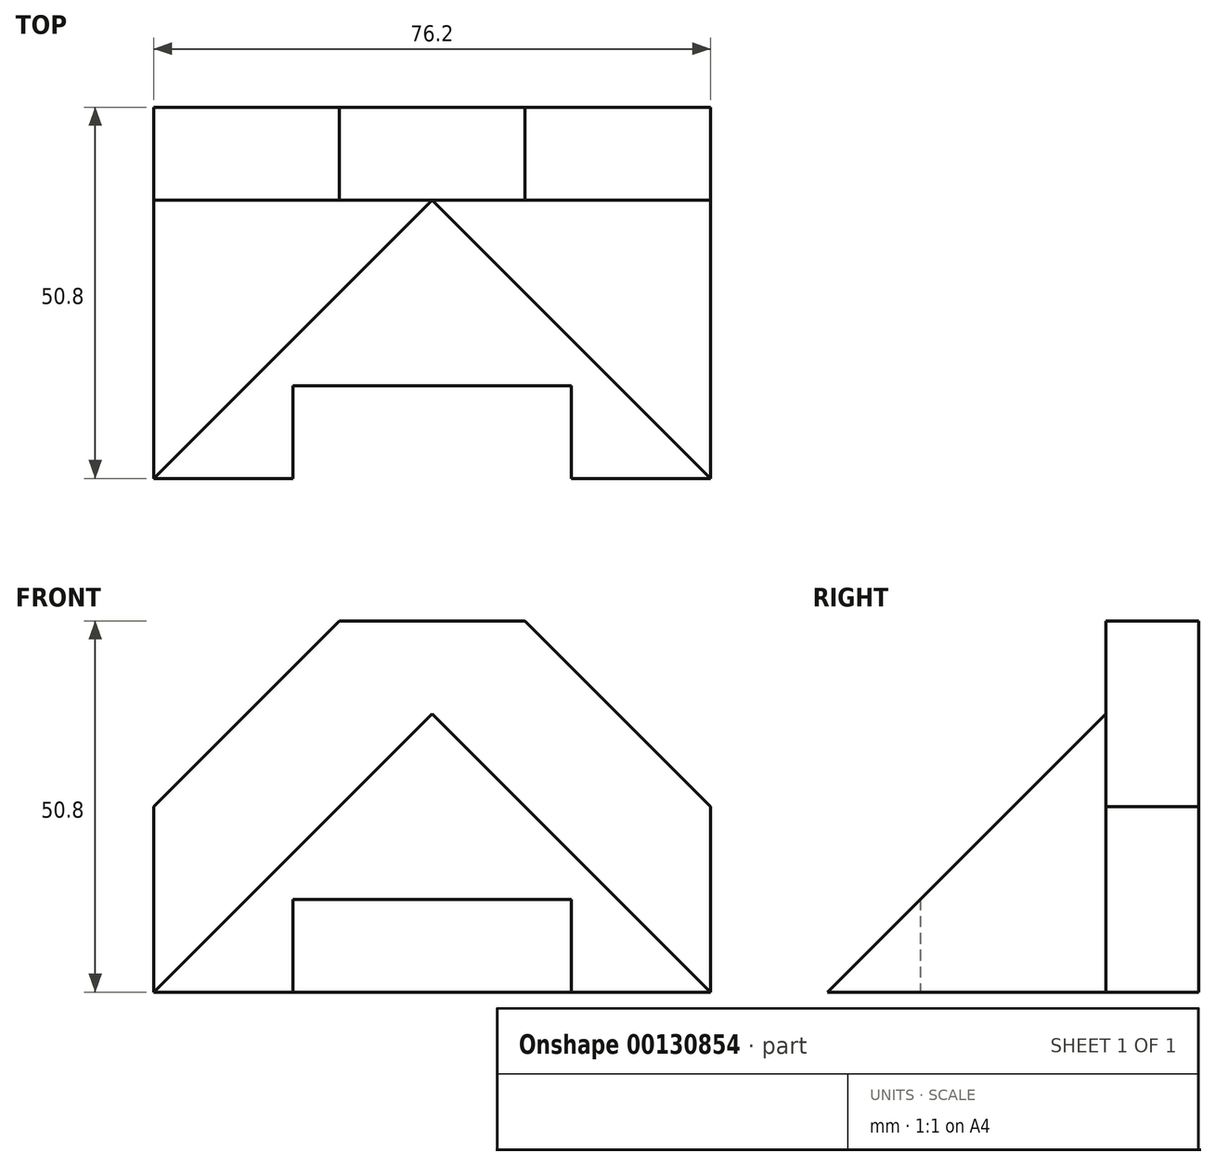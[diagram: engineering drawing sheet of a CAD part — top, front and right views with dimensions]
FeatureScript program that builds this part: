
annotation { "Feature Type Name" : "Feature", "Feature Type Description" : "" }
export const myFeature = defineFeature(function(context is Context, id is Id, definition is map)
    precondition{}
    {
        {
            var Q0;
            Q0=qCreatedBy(makeId("Right.planeOp"),FACE);
            var sketch = newSketch(context, id + "F0", { "sketchPlane" : qUnion([Q0])});
            skLineSegment(sketch, "E0", {"start": v(0, 0) * mm, "end": v(38.1, 0) * mm});
            skLineSegment(sketch, "E1", {"start": v(38.1, 0) * mm, "end": v(38.1, 38.1) * mm});
            skLineSegment(sketch, "E2", {"start": v(38.1, 38.1) * mm, "end": v(0, 0) * mm});
            skLineSegment(sketch, "E3", {"start": v(38.1, 38.1) * mm, "end": v(38.1, 50.8) * mm});
            skLineSegment(sketch, "E4", {"start": v(38.1, 50.8) * mm, "end": v(50.8, 50.8) * mm});
            skLineSegment(sketch, "E5", {"start": v(50.8, 50.8) * mm, "end": v(50.8, 0) * mm});
            skLineSegment(sketch, "E6", {"start": v(50.8, 0) * mm, "end": v(38.1, 0) * mm});
            skLineSegment(sketch, "E7", {"start": v(0, 0) * mm, "end": v(0, 38.1) * mm});
            skLineSegment(sketch, "E8", {"start": v(0, 38.1) * mm, "end": v(38.1, 38.1) * mm});
            skSolve(sketch);
        }
        {
            var Q0;
            Q0=makeQuery(id+"F0.imprint","IMPRINT",FACE,{"disambiguationData":[TD([[makeQuery(id+"F0.imprint","IMPRINT",EDGE,{"derivedFrom":sQuery(id+"F0.wireOp",EDGE,"E1")}),-1.0]])]});
            extrude(context, id + "F1", {"entities" : qUnion([Q0]), "endBound" : BoundingType.SYMMETRIC, "depth" : 76.2 * mm});
        }
        {
            var Q0;
            Q0=makeQuery(id+"F1.opExtrude","SWEPT_FACE",FACE,{"disambiguationData":[OSD([sQuery(id+"F0.wireOp",EDGE,"E1"),sQuery(id+"F0.wireOp",EDGE,"E3")])]});
            var sketch = newSketch(context, id + "F2", { "sketchPlane" : qUnion([Q0])});
            skLineSegment(sketch, "E9", {"start": v(0, 50.8) * mm, "end": v(-12.7, 50.8) * mm});
            skLineSegment(sketch, "E10", {"start": v(-12.7, 50.8) * mm, "end": v(-38.1, 25.4) * mm});
            skLineSegment(sketch, "E11", {"start": v(0, 50.8) * mm, "end": v(12.7, 50.8) * mm});
            skLineSegment(sketch, "E12", {"start": v(12.7, 50.8) * mm, "end": v(38.1, 25.4) * mm});
            skSolve(sketch);
        }
        {
            var Q0;
            {var subQ0=sQuery(id+"F2.wireOp",EDGE,"E10");Q0=makeQuery(id+"F2.imprint","IMPRINT",FACE,{"disambiguationData":[TD([[makeQuery(id+"F2.imprint","IMPRINT",EDGE,{"derivedFrom":subQ0}),-1.0]])]});}
            var Q1;
            {var subQ0=sQuery(id+"F2.wireOp",EDGE,"E12");Q1=makeQuery(id+"F2.imprint","IMPRINT",FACE,{"disambiguationData":[TD([[makeQuery(id+"F2.imprint","IMPRINT",EDGE,{"derivedFrom":subQ0}),1.0]])]});}
            extrude(context, id + "F3", {"entities" : qUnion([Q0, Q1]), "operationType" : NewBodyOperationType.REMOVE, "oppositeDirection" : true, "depth" : 72.61 * mm});
        }
        {
            var Q0;
            Q0=makeQuery(id+"F1.opExtrude","SWEPT_FACE",FACE,{"disambiguationData":[OSD([sQuery(id+"F0.wireOp",EDGE,"E1"),sQuery(id+"F0.wireOp",EDGE,"E3")])]});
            var sketch = newSketch(context, id + "F4", { "sketchPlane" : qUnion([Q0])});
            skLineSegment(sketch, "E13", {"start": v(-38.1, 0) * mm, "end": v(-38.1, 38.1) * mm});
            skLineSegment(sketch, "E14", {"start": v(-38.1, 38.1) * mm, "end": v(38.1, 38.1) * mm});
            skLineSegment(sketch, "E15", {"start": v(38.1, 38.1) * mm, "end": v(38.1, 0) * mm});
            skSolve(sketch);
        }
        {
            var Q0;
            {var subQ0=sQuery(id+"F4.wireOp",EDGE,"E13");var subQ1=makeQuery(id+"F3.boolean.opBoolean","COPY",EDGE,{"derivedFrom":makeQuery(id+"F3.opExtrude","CAP_EDGE",EDGE,{"disambiguationData":[OSD([sQuery(id+"F2.wireOp",EDGE,"E10")])],"isStart":true})});var subQ2=makeQuery(id+"F4.imprint","INTERSECT",VERTEX,{"derivedFrom":[subQ1,subQ0]});Q0=makeQuery(id+"F4.imprint","IMPRINT",FACE,{"disambiguationData":[TD([[makeQuery(id+"F4.imprint","IMPRINT",EDGE,{"disambiguationData":[TD([[subQ2,-1.0]])],"derivedFrom":subQ0}),-1.0]])]});}
            var Q1;
            {var subQ0=makeQuery(id+"F1.opExtrude","SWEPT_EDGE",EDGE,{"disambiguationData":[OSD([sQuery(id+"F0.wireOp",EDGE,"E0"),sQuery(id+"F0.wireOp",EDGE,"E1"),sQuery(id+"F0.wireOp",EDGE,"E6")])]});Q1=makeQuery(id+"F4.imprint","IMPRINT",FACE,{"disambiguationData":[TD([[makeQuery(id+"F4.imprint","IMPRINT",EDGE,{"derivedFrom":subQ0}),-1.0]])]});}
            var Q2;
            {var subQ0=sQuery(id+"F4.wireOp",EDGE,"E15");var subQ1=sQuery(id+"F4.wireOp",EDGE,"E14");var subQ2=makeQuery(id+"F4.imprint","INTERSECT",VERTEX,{"derivedFrom":[subQ1,subQ0]});Q2=makeQuery(id+"F4.imprint","IMPRINT",FACE,{"disambiguationData":[TD([[makeQuery(id+"F4.imprint","IMPRINT",EDGE,{"disambiguationData":[TD([[subQ2,1.0]])],"derivedFrom":subQ1}),-1.0]])]});}
            extrude(context, id + "F5", {"entities" : qUnion([Q0, Q1, Q2]), "operationType" : NewBodyOperationType.ADD, "depth" : 38.1 * mm});
        }
        {
            var Q0;
            Q0=makeQuery(id+"F5.opExtrude","CAP_FACE",FACE,{"disambiguationData":[OSD([sQuery(id+"F0.wireOp",EDGE,"E0"),sQuery(id+"F0.wireOp",EDGE,"E1"),sQuery(id+"F0.wireOp",EDGE,"E6"),sQuery(id+"F4.wireOp",EDGE,"E13"),sQuery(id+"F4.wireOp",EDGE,"E14"),sQuery(id+"F4.wireOp",EDGE,"E15")])],"isStart":false});
            var sketch = newSketch(context, id + "F6", { "sketchPlane" : qUnion([Q0])});
            skLineSegment(sketch, "E16", {"start": v(-38.1, 38.1) * mm, "end": v(0, 38.1) * mm});
            skLineSegment(sketch, "E17", {"start": v(0, 38.1) * mm, "end": v(-38.1, 0) * mm});
            skLineSegment(sketch, "E18", {"start": v(38.1, 38.1) * mm, "end": v(0, 38.1) * mm});
            skLineSegment(sketch, "E19", {"start": v(38.1, 0) * mm, "end": v(0, 38.1) * mm});
            skSolve(sketch);
        }
        {
            var Q0;
            Q0=makeQuery(id+"F6.imprint","IMPRINT",FACE,{"disambiguationData":[TD([[makeQuery(id+"F6.imprint","IMPRINT",EDGE,{"derivedFrom":sQuery(id+"F6.wireOp",EDGE,"E16")}),-1.0]])]});
            var Q1;
            Q1=makeQuery(id+"F6.imprint","IMPRINT",FACE,{"disambiguationData":[TD([[makeQuery(id+"F6.imprint","IMPRINT",EDGE,{"derivedFrom":sQuery(id+"F6.wireOp",EDGE,"E18")}),-1.0]])]});
            extrude(context, id + "F7", {"entities" : qUnion([Q0, Q1]), "operationType" : NewBodyOperationType.REMOVE, "oppositeDirection" : true, "depth" : 38.1 * mm});
        }
        {
            var Q0;
            Q0=makeQuery(id+"F0.imprint","IMPRINT",FACE,{"disambiguationData":[TD([[makeQuery(id+"F0.imprint","IMPRINT",EDGE,{"derivedFrom":sQuery(id+"F0.wireOp",EDGE,"E2")}),-1.0]])]});
            extrude(context, id + "F8", {"entities" : qUnion([Q0]), "operationType" : NewBodyOperationType.REMOVE, "endBound" : BoundingType.SYMMETRIC, "depth" : 76.2 * mm});
        }
        {
            var Q0;
            {var subQ0=sQuery(id+"F0.wireOp",EDGE,"E6");Q0=makeQuery(id+"F5.boolean.opBoolean","MERGE",FACE,{"derivedFrom":[makeQuery(id+"F1.opExtrude","SWEPT_FACE",FACE,{"disambiguationData":[OSD([subQ0])]}),makeQuery(id+"F5.opExtrude","SWEPT_FACE",FACE,{"disambiguationData":[OSD([sQuery(id+"F0.wireOp",EDGE,"E0"),sQuery(id+"F0.wireOp",EDGE,"E1"),subQ0])]})]});}
            var sketch = newSketch(context, id + "F9", { "sketchPlane" : qUnion([Q0])});
            skLineSegment(sketch, "E20", {"start": v(0, 0) * mm, "end": v(-19.05, 0) * mm});
            skLineSegment(sketch, "E21", {"start": v(-19.05, 0) * mm, "end": v(-19.05, -12.7) * mm});
            skLineSegment(sketch, "E22", {"start": v(-19.05, -12.7) * mm, "end": v(19.05, -12.7) * mm});
            skLineSegment(sketch, "E23", {"start": v(19.05, -12.7) * mm, "end": v(19.05, 0) * mm});
            skLineSegment(sketch, "E24", {"start": v(19.05, 0) * mm, "end": v(0, 0) * mm});
            skSolve(sketch);
        }
        {
            var Q0;
            Q0=makeQuery(id+"F9.imprint","IMPRINT",FACE,{"disambiguationData":[TD([[makeQuery(id+"F9.imprint","IMPRINT",EDGE,{"derivedFrom":sQuery(id+"F9.wireOp",EDGE,"E20")}),1.0]])]});
            extrude(context, id + "F10", {"entities" : qUnion([Q0]), "operationType" : NewBodyOperationType.REMOVE, "oppositeDirection" : true, "depth" : 33.88 * mm});
        }
    });
